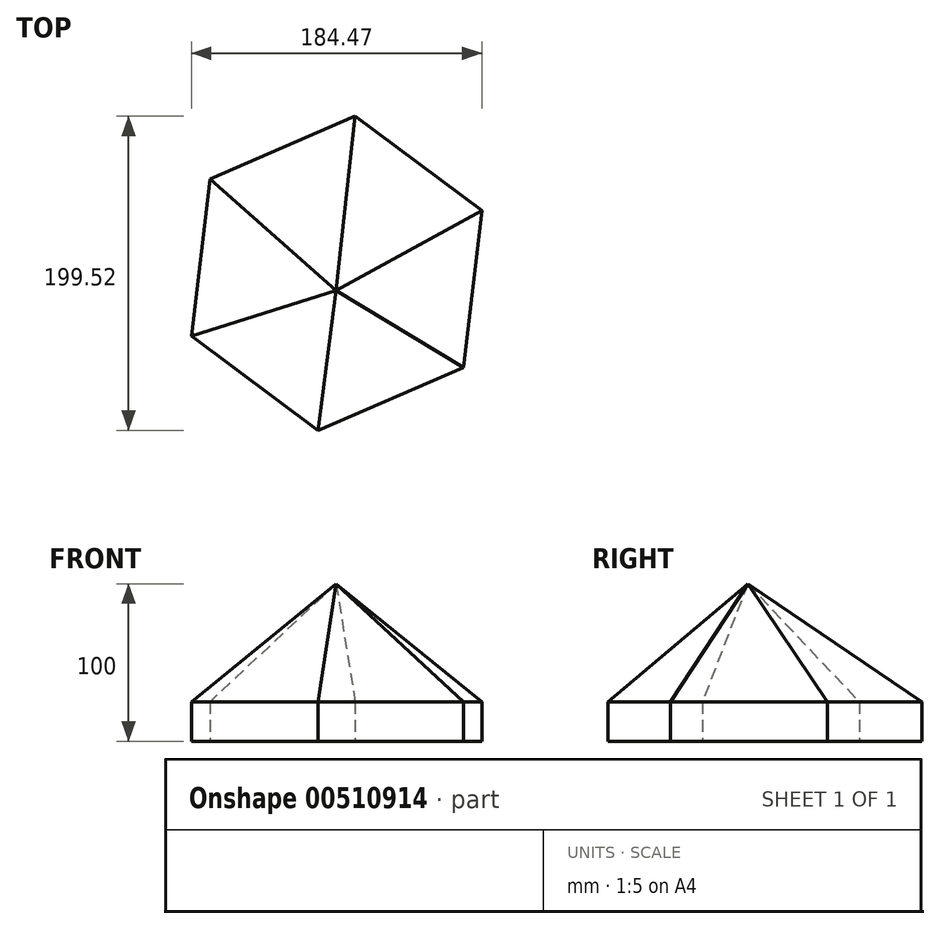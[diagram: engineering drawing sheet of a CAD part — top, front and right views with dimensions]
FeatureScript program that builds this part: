
annotation { "Feature Type Name" : "Feature", "Feature Type Description" : "" }
export const myFeature = defineFeature(function(context is Context, id is Id, definition is map)
    precondition{}
    {
        {
            var Q0;
            Q0=qCreatedBy(makeId("Top.planeOp"),FACE);
            var sketch = newSketch(context, id + "F0", { "sketchPlane" : qUnion([Q0])});
            skCircle(sketch, "E0.cCircle", {"center": v(-0.57, 13.34) * mm, "radius": 100.44 * mm, "construction": true});
            skLineSegment(sketch, "E0.0", {"start": v(-12.25, -86.42) * mm, "end": v(-92.8, -26.43) * mm});
            skLineSegment(sketch, "E0.1", {"start": v(-92.8, -26.43) * mm, "end": v(-81.13, 73.33) * mm});
            skLineSegment(sketch, "E0.2", {"start": v(-81.13, 73.33) * mm, "end": v(11.1, 113.1) * mm});
            skLineSegment(sketch, "E0.3", {"start": v(11.1, 113.1) * mm, "end": v(91.66, 53.1) * mm});
            skLineSegment(sketch, "E0.4", {"start": v(91.66, 53.1) * mm, "end": v(79.98, -46.65) * mm});
            skLineSegment(sketch, "E0.5", {"start": v(79.98, -46.65) * mm, "end": v(-12.25, -86.42) * mm});
            skSolve(sketch);
        }
        {
            var Q0;
            Q0 = qSketchRegion(id + "F0", true);
            extrude(context, id + "F1", {"entities" : qUnion([Q0]), "depth" : 25 * mm});
        }
        {
            var Q0;
            Q0=qCreatedBy(makeId("Top.planeOp"),FACE);
            cPlane(context, id + "F2", {"entities" : qUnion([Q0]), "cplaneType" : CPlaneType.OFFSET, "offset" : 100 * mm, "width" : 150 * mm, "height" : 150 * mm});
        }
        {
            var Q0;
            Q0=qCreatedBy(id+"F2.planeOp",FACE);
            var sketch = newSketch(context, id + "F3", { "sketchPlane" : qUnion([Q0])});
            skPoint(sketch, "E1", {"position": v(-0.96, 2.46) * mm});
            skSolve(sketch);
        }
        {
            var Q1;
            Q1=sQuery(id+"F3.wireOp",VERTEX,"E1");
            var Q2;
            Q2=makeQuery(id+"F1.opExtrude","CAP_FACE",FACE,{"disambiguationData":[OSD([sQuery(id+"F0.wireOp",EDGE,"E0.0"),sQuery(id+"F0.wireOp",EDGE,"E0.1"),sQuery(id+"F0.wireOp",EDGE,"E0.2"),sQuery(id+"F0.wireOp",EDGE,"E0.3"),sQuery(id+"F0.wireOp",EDGE,"E0.4"),sQuery(id+"F0.wireOp",EDGE,"E0.5")])],"isStart":false});
            loft(context, id + "F4", {"operationType" : NewBodyOperationType.ADD, "sheetProfilesArray" : [{ "sheetProfileEntities" : qUnion([Q1]) }, { "sheetProfileEntities" : qUnion([Q2]) }]});
        }
    });
